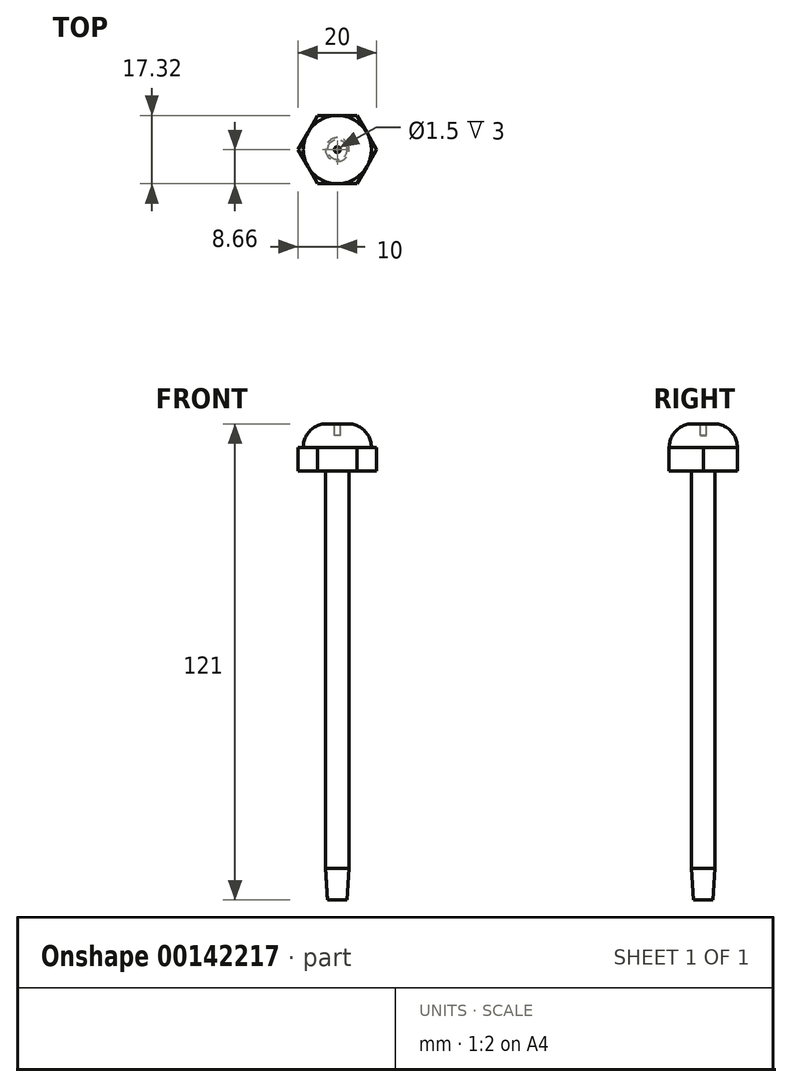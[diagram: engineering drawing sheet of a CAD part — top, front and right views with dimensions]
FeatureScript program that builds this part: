
annotation { "Feature Type Name" : "Feature", "Feature Type Description" : "" }
export const myFeature = defineFeature(function(context is Context, id is Id, definition is map)
    precondition{}
    {
        {
            var Q0;
            Q0=qCreatedBy(makeId("Top.planeOp"),FACE);
            var sketch = newSketch(context, id + "F0", { "sketchPlane" : qUnion([Q0])});
            skCircle(sketch, "E0", {"center": v(0, 0) * mm, "radius": 3 * mm});
            skLineSegment(sketch, "E1", {"start": v(-5, 8.66) * mm, "end": v(5, 8.66) * mm});
            skLineSegment(sketch, "E2", {"start": v(5, 8.66) * mm, "end": v(10, 0) * mm});
            skLineSegment(sketch, "E3", {"start": v(10, 0) * mm, "end": v(5, -8.66) * mm});
            skLineSegment(sketch, "E4", {"start": v(5, -8.66) * mm, "end": v(-5, -8.66) * mm});
            skLineSegment(sketch, "E5", {"start": v(-5, -8.66) * mm, "end": v(-10, 0) * mm});
            skLineSegment(sketch, "E6", {"start": v(-5, 8.66) * mm, "end": v(-10, 0) * mm});
            skLineSegment(sketch, "E7", {"start": v(-5, 8.66) * mm, "end": v(5, -8.66) * mm, "construction": true});
            skSolve(sketch);
        }
        {
            var Q0;
            Q0=qSketchRegion(id+"F0",true);
            var Q1;
            Q1=makeQuery(id+"F0.imprint","IMPRINT",FACE,{"disambiguationData":[TD([[makeQuery(id+"F0.imprint","IMPRINT",EDGE,{"derivedFrom":sQuery(id+"F0.wireOp",EDGE,"E0")}),1.0]])]});
            extrude(context, id + "F1", {"entities" : qUnion([Q0, Q1]), "depth" : 6 * mm});
        }
        {
            var Q0;
            Q0=makeQuery(id+"F1.opExtrude","CAP_FACE",FACE,{"disambiguationData":[OSD([sQuery(id+"F0.wireOp",EDGE,"E1"),sQuery(id+"F0.wireOp",EDGE,"E2"),sQuery(id+"F0.wireOp",EDGE,"E3"),sQuery(id+"F0.wireOp",EDGE,"E4"),sQuery(id+"F0.wireOp",EDGE,"E5"),sQuery(id+"F0.wireOp",EDGE,"E6")])],"isStart":false});
            var sketch = newSketch(context, id + "F2", { "sketchPlane" : qUnion([Q0])});
            skCircle(sketch, "E8", {"center": v(0, 0) * mm, "radius": 8.66 * mm});
            skSolve(sketch);
        }
        {
            var Q0;
            Q0=qSketchRegion(id+"F2",true);
            extrude(context, id + "F3", {"entities" : qUnion([Q0]), "operationType" : NewBodyOperationType.ADD, "depth" : 6 * mm});
        }
        {
            var Q0;
            Q0=makeQuery(id+"F3.opExtrude","CAP_EDGE",EDGE,{"disambiguationData":[OSD([sQuery(id+"F2.wireOp",EDGE,"E8")])],"isStart":false});
            fillet(context, id + "F4", {"entities" : qUnion([Q0]), "radius" : 6 * mm, "tangentPropagation" : true, "allowEdgeOverflow" : false});
        }
        {
            var Q0;
            Q0=makeQuery(id+"F3.opExtrude","CAP_FACE",FACE,{"disambiguationData":[OSD([sQuery(id+"F2.wireOp",EDGE,"E8")])],"isStart":false});
            var sketch = newSketch(context, id + "F5", { "sketchPlane" : qUnion([Q0])});
            skCircle(sketch, "E9", {"center": v(0, 0) * mm, "radius": 0.75 * mm});
            skSolve(sketch);
        }
        {
            var Q0;
            Q0=qSketchRegion(id+"F5",true);
            extrude(context, id + "F6", {"entities" : qUnion([Q0]), "operationType" : NewBodyOperationType.REMOVE, "oppositeDirection" : true, "depth" : 3 * mm});
        }
        {
            var Q0;
            Q0=makeQuery(id+"F1.opExtrude","CAP_FACE",FACE,{"disambiguationData":[OSD([sQuery(id+"F0.wireOp",EDGE,"E1"),sQuery(id+"F0.wireOp",EDGE,"E2"),sQuery(id+"F0.wireOp",EDGE,"E3"),sQuery(id+"F0.wireOp",EDGE,"E4"),sQuery(id+"F0.wireOp",EDGE,"E5"),sQuery(id+"F0.wireOp",EDGE,"E6")])],"isStart":true});
            var sketch = newSketch(context, id + "F7", { "sketchPlane" : qUnion([Q0])});
            skCircle(sketch, "E10", {"center": v(0, 0) * mm, "radius": 3 * mm});
            skSolve(sketch);
        }
        {
            var Q0;
            Q0=makeQuery(id+"F7.imprint","IMPRINT",FACE,{"disambiguationData":[TD([[makeQuery(id+"F7.imprint","IMPRINT",EDGE,{"derivedFrom":sQuery(id+"F7.wireOp",EDGE,"E10")}),1.0]])]});
            extrude(context, id + "F8", {"entities" : qUnion([Q0]), "operationType" : NewBodyOperationType.ADD, "depth" : 101 * mm});
        }
        {
            var Q0;
            Q0=makeQuery(id+"F8.opExtrude","CAP_FACE",FACE,{"disambiguationData":[OSD([sQuery(id+"F7.wireOp",EDGE,"E10")])],"isStart":false});
            var Q1;
            Q1 = qBodyType(qCreatedBy(id + "F11" ,EDGE), BodyType.WIRE);
            cPlane(context, id + "F9", {"entities" : qUnion([Q0, Q1]), "cplaneType" : CPlaneType.OFFSET, "offset" : 8 * mm, "width" : 150 * mm, "height" : 150 * mm});
        }
        {
            var Q0;
            Q0=qCreatedBy(id+"F9.planeOp",FACE);
            var sketch = newSketch(context, id + "F10", { "sketchPlane" : qUnion([Q0])});
            skCircle(sketch, "E11", {"center": v(0, 0) * mm, "radius": 2.5 * mm});
            skSolve(sketch);
        }
        {
            var Q0;
            Q0=makeQuery(id+"F8.opExtrude","CAP_FACE",FACE,{"disambiguationData":[OSD([sQuery(id+"F7.wireOp",EDGE,"E10")])],"isStart":false});
            var sketch = newSketch(context, id + "F11", { "sketchPlane" : qUnion([Q0])});
            skCircle(sketch, "E12", {"center": v(0, 0) * mm, "radius": 3 * mm});
            skSolve(sketch);
        }
        {
            var Q1;
            Q1=qSketchRegion(id+"F10",true);
            var Q2;
            Q2=qSketchRegion(id+"F11",true);
            loft(context, id + "F12", {"operationType" : NewBodyOperationType.ADD, "sheetProfilesArray" : [{ "sheetProfileEntities" : qUnion([Q1]) }, { "sheetProfileEntities" : qUnion([Q2]) }]});
        }
    });
